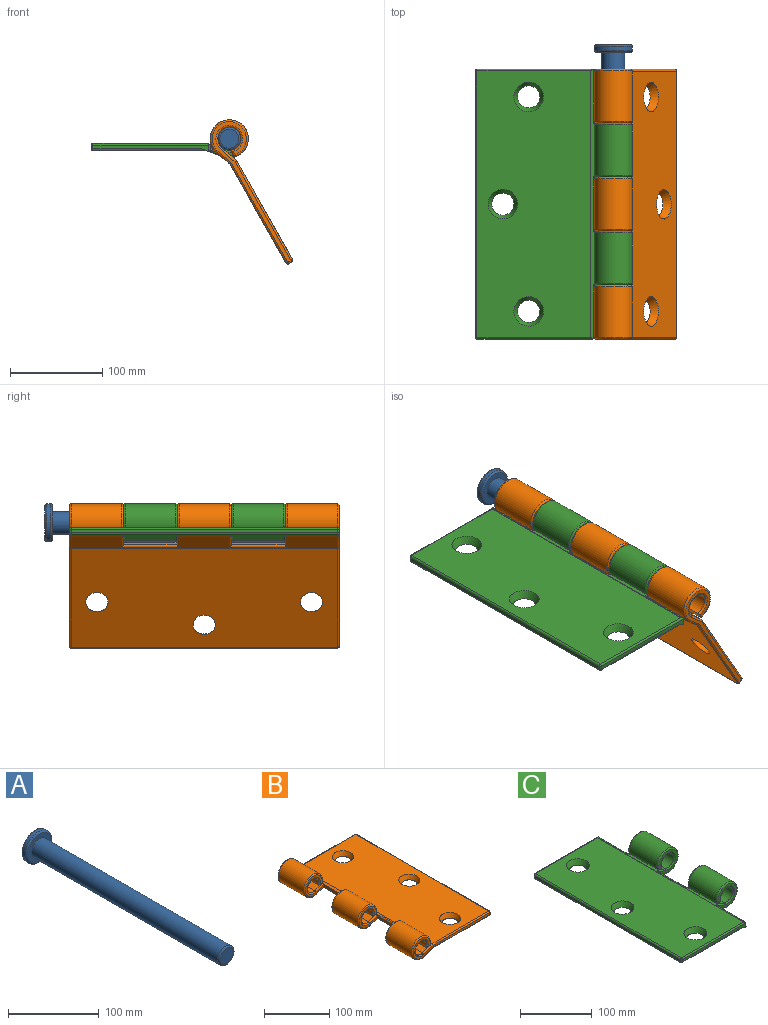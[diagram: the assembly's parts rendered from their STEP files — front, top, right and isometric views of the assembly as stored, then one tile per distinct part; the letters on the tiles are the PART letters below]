
ASSEMBLY  parts=3 mates=2
PART A: 8 faces, bbox 44.4x300x44.4 mm
  f0: cylinder r=12.25mm len=290mm, axis (0,1,0), area 22321mm2, adj f4,f7
  f1: plane 20.5x20.5mm, normal (0,-1,0), area 330.1mm2, adj f7
  f2: cylinder r=20.5mm len=41mm, axis (0,-1,0), area 515.2mm2, adj f5,f6
  f3: plane 37x37mm, normal (0,1,0), area 1075.2mm2, adj f6
  f4: plane 37x37mm, normal (0,-1,0), area 603.8mm2, adj f0,f5
  f5: torus R=18.5mm, axis (0,1,0), area 390.3mm2, adj f2,f4
  f6: torus R=18.5mm, axis (0,1,0), area 390.3mm2, adj f2,f3
  f7: torus R=10.25mm, axis (0,1,0), area 227.5mm2, adj f0,f1
PART B: 69 faces, bbox 171.7x292x44.4 mm
  f0: cylinder r=12.5mm len=54.4mm, axis (0,1,0), area 3703.3mm2, adj f4,f7,f27,f36
  f1: cylinder r=12.5mm len=54.4mm, axis (0,1,0), area 3703.3mm2, adj f5,f7,f35,f67
  f2: cylinder r=20.5mm len=54.4mm, axis (0,1,0), area 5913.6mm2, adj f4,f11,f25,f39
  f3: cylinder r=20.5mm len=54.4mm, axis (0,1,0), area 5913.6mm2, adj f5,f11,f32,f53
  f4: plane 56.4x8.42mm, normal (0,0,-1), area 473.3mm2, adj f0,f2,f24,f25,f27,f37
  f5: plane 56.4x8.42mm, normal (0,0,-1), area 473.3mm2, adj f1,f3,f21,f34,f53,f67
  f6: cylinder r=12.5mm len=54.4mm, axis (0,1,0), area 3703.3mm2, adj f7,f13,f41,f66
  f7: plane 288x20.54mm, normal (-0.32,0,0.95), area 3970.7mm2, adj f0,f1,f6,f8,f19,f29,f31,f33
  f8: plane 288x123mm, normal (0,0,1), area 33011.3mm2, adj f7,f16,f17,f18,f40,f47,f48
  f9: plane 288x4mm, normal (1,0,0), area 1152mm2, adj f46,f47,f51,f52
  f10: plane 288x123mm, normal (0,0,-1), area 34066.8mm2, adj f11,f16,f17,f18,f45,f51,f56
  f11: plane 288x17.59mm, normal (0.34,0,-0.94), area 3224.6mm2, adj f2,f3,f10,f12,f26,f28,f30,f42
  f12: cylinder r=20.5mm len=54.4mm, axis (0,1,0), area 5820.5mm2, adj f11,f60,f61,f62
  f13: plane 56.4x6.8mm, normal (0,0,-1), area 382.5mm2, adj f6,f15,f41,f60,f62,f65
  f14: plane 166x37mm, normal (0,-1,0), area 913.5mm2, adj f36,f37,f38,f39,f40,f42,f45,f46
  f15: plane 166x37mm, normal (0,1,0), area 921.7mm2, adj f13,f41,f44,f48,f52,f56,f58,f60
  f16: cone r=12mm half-angle=26.6deg, axis (0,0,1), area 786.8mm2, adj f8,f10
  f17: cone r=12mm half-angle=26.6deg, axis (0,0,1), area 786.8mm2, adj f8,f10
  f18: cone r=12mm half-angle=26.6deg, axis (0,0,1), area 786.8mm2, adj f8,f10
  f19: plane 62.4x5.26mm, normal (-1,0,0), area 308.8mm2, adj f7,f20,f21,f57,f64,f68
  f20: plane 39.12x37mm, normal (0,-1,0), area 406.2mm2, adj f19,f57,f59,f61,f64,f65,f66
  f21: plane 39.12x37mm, normal (0,1,0), area 414.5mm2, adj f5,f19,f53,f55,f57,f67,f68
  f22: plane 58.61x3.82mm, normal (-1,0,0), area 222.9mm2, adj f23,f24,f28,f29,f31,f33
  f23: plane 39.12x37mm, normal (0,-1,0), area 406.2mm2, adj f22,f28,f30,f32,f33,f34,f35
  f24: plane 39.12x37mm, normal (0,1,0), area 414.5mm2, adj f4,f22,f25,f26,f27,f28,f29
  f25: torus R=18.5mm, axis (0,1,0), area 330mm2, adj f2,f4,f24,f26
  f26: cylinder r=2mm len=16.94mm, axis (0.94,0,0.34), area 50.3mm2, adj f11,f24,f25,f28
  f27: torus R=14.5mm, axis (0,1,0), area 225.3mm2, adj f0,f4,f24,f29
  f28: cylinder r=2mm len=62.4mm, axis (0,1,0), area 228.2mm2, adj f11,f22,f23,f24,f26,f30
  f29: cylinder r=2mm len=18.54mm, axis (-0.95,0,-0.32), area 55.3mm2, adj f7,f22,f24,f27,f31
  f30: cylinder r=2mm len=16.94mm, axis (-0.94,0,-0.34), area 50.3mm2, adj f11,f23,f28,f32
  f31: cylinder r=2mm len=62.4mm, axis (0,-1,0), area 150.4mm2, adj f7,f22,f29,f33
  f32: torus R=18.5mm, axis (0,1,0), area 327.6mm2, adj f3,f23,f30,f34
  f33: cylinder r=2mm len=18.54mm, axis (0.95,0,0.32), area 55.3mm2, adj f7,f22,f23,f31,f35
  f34: cylinder r=2mm len=8.42mm, axis (-1,0,0), area 21.4mm2, adj f5,f23,f32,f35
  f35: torus R=14.5mm, axis (0,1,0), area 222.9mm2, adj f1,f23,f33,f34
  f36: torus R=14.5mm, axis (0,-1,0), area 222.9mm2, adj f0,f14,f37,f38
  f37: cylinder r=2mm len=8.42mm, axis (1,0,0), area 21.4mm2, adj f4,f14,f36,f39
  f38: cylinder r=2mm len=21.18mm, axis (-0.95,0,-0.32), area 67.7mm2, adj f7,f14,f36,f40
  f39: torus R=18.5mm, axis (0,-1,0), area 327.6mm2, adj f2,f14,f37,f42
  f40: cylinder r=2mm len=123mm, axis (-1,0,0), area 386mm2, adj f8,f14,f38,f43
  f41: torus R=14.5mm, axis (0,-1,0), area 225.3mm2, adj f6,f13,f15,f44
  f42: cylinder r=2mm len=18.59mm, axis (0.94,0,0.34), area 59.1mm2, adj f11,f14,f39,f45
  f43: sphere r=2mm, area 6.3mm2, adj f40,f46,f47
  f44: cylinder r=2mm len=21.18mm, axis (0.95,0,0.32), area 67.7mm2, adj f7,f15,f41,f48
  f45: cylinder r=2mm len=123.35mm, axis (1,0,0), area 386.8mm2, adj f10,f14,f42,f49
  f46: cylinder r=2mm len=4mm, axis (0,0,1), area 12.6mm2, adj f9,f14,f43,f49
  f47: cylinder r=2mm len=288mm, axis (0,1,0), area 904.8mm2, adj f8,f9,f43,f50
  f48: cylinder r=2mm len=123mm, axis (1,0,0), area 386mm2, adj f8,f15,f44,f50
  f49: sphere r=2mm, area 6.3mm2, adj f45,f46,f51
  f50: sphere r=2mm, area 6.3mm2, adj f47,f48,f52
  f51: cylinder r=2mm len=288mm, axis (0,1,0), area 904.8mm2, adj f9,f10,f49,f54
  f52: cylinder r=2mm len=4mm, axis (0,0,-1), area 12.6mm2, adj f9,f15,f50,f54
  f53: torus R=18.5mm, axis (0,1,0), area 330mm2, adj f3,f5,f21,f55
  f54: sphere r=2mm, area 6.3mm2, adj f51,f52,f56
  f55: cylinder r=2mm len=16.94mm, axis (0.94,0,0.34), area 50.3mm2, adj f11,f21,f53,f57
  f56: cylinder r=2mm len=123.35mm, axis (-1,0,0), area 386.8mm2, adj f10,f15,f54,f58
  f57: cylinder r=2mm len=62.4mm, axis (0,1,0), area 228.2mm2, adj f11,f19,f20,f21,f55,f59
  f58: cylinder r=2mm len=18.59mm, axis (-0.94,0,-0.34), area 59.1mm2, adj f11,f15,f56,f60
  f59: cylinder r=2mm len=16.94mm, axis (-0.94,0,-0.34), area 50.3mm2, adj f11,f20,f57,f61
  f60: torus R=18.5mm, axis (0,-1,0), area 328.3mm2, adj f12,f13,f15,f58,f62
  f61: torus R=18.5mm, axis (0,1,0), area 324.2mm2, adj f12,f20,f59,f63
  f62: cylinder r=2mm len=56.35mm, axis (0,1,0), area 156.4mm2, adj f12,f13,f60,f63
  f63: sphere r=2mm, area 5.6mm2, adj f61,f62,f65
  f64: cylinder r=2mm len=17.18mm, axis (0.95,0,0.32), area 54mm2, adj f7,f19,f20,f66
  f65: cylinder r=2mm len=6.8mm, axis (-1,0,0), area 18.1mm2, adj f13,f20,f63,f66
  f66: torus R=14.5mm, axis (0,1,0), area 222.9mm2, adj f6,f20,f64,f65
  f67: torus R=14.5mm, axis (0,1,0), area 225.3mm2, adj f1,f5,f21,f68
  f68: cylinder r=2mm len=17.18mm, axis (-0.95,0,-0.32), area 54mm2, adj f7,f19,f21,f67
PART C: 74 faces, bbox 171.7x292x44.4 mm
  f0: cylinder r=12.5mm len=54.4mm, axis (0,1,0), area 3703.3mm2, adj f2,f6,f27,f61
  f1: cylinder r=12.5mm len=54.4mm, axis (0,1,0), area 3703.3mm2, adj f2,f7,f33,f43
  f2: plane 291.31x20.23mm, normal (0.32,0,0.95), area 2780.8mm2, adj f0,f1,f28,f29,f30,f31,f32,f46
  f3: plane 292x23.17mm, normal (-0.34,0,-0.94), area 2310.2mm2, adj f4,f5,f8,f9,f12,f35,f36,f37
  f4: cylinder r=20.5mm len=54.4mm, axis (0,1,0), area 5913.6mm2, adj f3,f6,f34,f54
  f5: cylinder r=20.5mm len=54.4mm, axis (0,1,0), area 5913.6mm2, adj f3,f7,f40,f42
  f6: plane 56.4x8.42mm, normal (0,0,-1), area 473.3mm2, adj f0,f4,f19,f27,f34,f55
  f7: plane 56.4x8.42mm, normal (0,0,-1), area 473.3mm2, adj f1,f5,f20,f33,f40,f41
  f8: plane 125x6.59mm, normal (0,-1,0), area 510.3mm2, adj f3,f45,f50,f51,f57,f62
  f9: plane 125x6.59mm, normal (0,1,0), area 510.3mm2, adj f3,f53,f64,f69,f71,f72
  f10: plane 288x122.68mm, normal (0,0,1), area 32917.7mm2, adj f13,f14,f15,f62,f63,f67,f71
  f11: plane 288x4mm, normal (-1,0,0), area 1152mm2, adj f51,f52,f63,f64
  f12: plane 288x123mm, normal (0,0,-1), area 34066.8mm2, adj f3,f13,f14,f15,f45,f52,f53
  f13: cone r=12mm half-angle=26.6deg, axis (0,0,1), area 786.8mm2, adj f10,f12
  f14: cone r=12mm half-angle=26.6deg, axis (0,0,1), area 786.8mm2, adj f10,f12
  f15: cone r=12mm half-angle=26.6deg, axis (0,0,1), area 786.8mm2, adj f10,f12
  f16: plane 37x37mm, normal (0,-1,0), area 398.4mm2, adj f23,f41,f42,f43,f44,f46
  f17: plane 54.4x3.82mm, normal (1,0,0), area 207.6mm2, adj f23,f50,f56,f57
  f18: plane 54.4x3.82mm, normal (1,0,0), area 207.6mm2, adj f24,f25,f30,f37
  f19: plane 37x37mm, normal (0,-1,0), area 406.7mm2, adj f6,f24,f27,f28,f34,f35
  f20: plane 37x37mm, normal (0,1,0), area 406.7mm2, adj f7,f25,f32,f33,f39,f40
  f21: plane 37x37mm, normal (0,1,0), area 398.4mm2, adj f26,f54,f55,f60,f61,f66
  f22: plane 54.4x3.82mm, normal (1,0,0), area 207.6mm2, adj f26,f69,f72,f73
  f23: cylinder r=2mm len=5.25mm, axis (0,0,-1), area 12.1mm2, adj f16,f17,f47,f49
  f24: cylinder r=2mm len=5.25mm, axis (0,0,-1), area 12.1mm2, adj f18,f19,f29,f36
  f25: cylinder r=2mm len=5.25mm, axis (0,0,1), area 12.1mm2, adj f18,f20,f31,f38
  f26: cylinder r=2mm len=5.25mm, axis (0,0,1), area 12.1mm2, adj f21,f22,f65,f70
  f27: torus R=14.5mm, axis (0,-1,0), area 225.3mm2, adj f0,f6,f19,f28
  f28: cylinder r=2mm len=14.54mm, axis (0.95,0,-0.32), area 46.1mm2, adj f2,f19,f27,f29
  f29: bspline ~4.7x4.17mm, area 12.7mm2, adj f2,f24,f28,f30
  f30: cylinder r=2mm len=54.4mm, axis (0,1,0), area 135.9mm2, adj f2,f18,f29,f31
  f31: bspline ~4.7x4mm, area 12.7mm2, adj f2,f25,f30,f32
  f32: cylinder r=2mm len=14.54mm, axis (-0.95,0,0.32), area 46.1mm2, adj f2,f20,f31,f33
  f33: torus R=14.5mm, axis (0,-1,0), area 225.3mm2, adj f1,f7,f20,f32
  f34: torus R=18.5mm, axis (0,-1,0), area 330mm2, adj f4,f6,f19,f35
  f35: cylinder r=2mm len=12.94mm, axis (-0.94,0,0.34), area 40.9mm2, adj f3,f19,f34,f36
  f36: bspline ~5.02x4.17mm, area 15.5mm2, adj f3,f24,f35,f37
  f37: cylinder r=2mm len=54.4mm, axis (0,-1,0), area 208.3mm2, adj f3,f18,f36,f38
  f38: bspline ~5.02x4mm, area 15.5mm2, adj f3,f25,f37,f39
  f39: cylinder r=2mm len=12.94mm, axis (0.94,0,-0.34), area 40.9mm2, adj f3,f20,f38,f40
  f40: torus R=18.5mm, axis (0,-1,0), area 330mm2, adj f5,f7,f20,f39
  f41: cylinder r=2mm len=8.42mm, axis (-1,0,0), area 21.4mm2, adj f7,f16,f42,f43
  f42: torus R=18.5mm, axis (0,-1,0), area 327.6mm2, adj f5,f16,f41,f44
  f43: torus R=14.5mm, axis (0,-1,0), area 222.9mm2, adj f1,f16,f41,f46
  f44: cylinder r=2mm len=12.94mm, axis (-0.94,0,0.34), area 40.9mm2, adj f3,f16,f42,f47
  f45: cylinder r=2mm len=123mm, axis (-1,0,0), area 380mm2, adj f3,f8,f12,f48
  f46: cylinder r=2mm len=14.54mm, axis (0.95,0,-0.32), area 46.1mm2, adj f2,f16,f43,f49
  f47: bspline ~5.02x4.17mm, area 15.5mm2, adj f3,f23,f44,f50
  f48: sphere r=2mm, area 6.3mm2, adj f45,f51,f52
  f49: bspline ~4.7x4.17mm, area 12.7mm2, adj f2,f23,f46,f56
  f50: cylinder r=2mm len=56.4mm, axis (0,-1,0), area 213.7mm2, adj f3,f8,f17,f47,f57
  f51: cylinder r=2mm len=4mm, axis (0,0,1), area 12.6mm2, adj f8,f11,f48,f58
  f52: cylinder r=2mm len=288mm, axis (0,1,0), area 904.8mm2, adj f11,f12,f48,f59
  f53: cylinder r=2mm len=123mm, axis (1,0,0), area 380mm2, adj f3,f9,f12,f59
  f54: torus R=18.5mm, axis (0,-1,0), area 327.6mm2, adj f4,f21,f55,f60
  f55: cylinder r=2mm len=8.42mm, axis (1,0,0), area 21.4mm2, adj f6,f21,f54,f61
  f56: cylinder r=2mm len=56.15mm, axis (0,1,0), area 138.5mm2, adj f2,f17,f49,f57,f62
  f57: cylinder r=2mm len=7.56mm, axis (0,0,1), area 19.3mm2, adj f8,f17,f50,f56,f62
  f58: sphere r=2mm, area 6.3mm2, adj f51,f62,f63
  f59: sphere r=2mm, area 6.3mm2, adj f52,f53,f64
  f60: cylinder r=2mm len=12.94mm, axis (0.94,0,-0.34), area 40.9mm2, adj f3,f21,f54,f65
  f61: torus R=14.5mm, axis (0,-1,0), area 222.9mm2, adj f0,f21,f55,f66
  f62: cylinder r=2mm len=125.97mm, axis (1,0,0), area 391.1mm2, adj f2,f8,f10,f56,f57,f58,f67
  f63: cylinder r=2mm len=288mm, axis (0,1,0), area 904.8mm2, adj f10,f11,f58,f68
  f64: cylinder r=2mm len=4mm, axis (0,0,-1), area 12.6mm2, adj f9,f11,f59,f68
  f65: bspline ~5.02x4mm, area 15.5mm2, adj f3,f26,f60,f69
  f66: cylinder r=2mm len=14.54mm, axis (-0.95,0,0.32), area 46.1mm2, adj f2,f21,f61,f70
  f67: cylinder r=2mm len=289.27mm, axis (0,-1,0), area 186mm2, adj f2,f10,f62,f71
  f68: sphere r=2mm, area 6.3mm2, adj f63,f64,f71
  f69: cylinder r=2mm len=56.4mm, axis (0,-1,0), area 213.7mm2, adj f3,f9,f22,f65,f72
  f70: bspline ~4.7x4mm, area 12.7mm2, adj f2,f26,f66,f73
  f71: cylinder r=2mm len=125.97mm, axis (-1,0,0), area 391.1mm2, adj f2,f9,f10,f67,f68,f72,f73
  f72: cylinder r=2mm len=7.56mm, axis (0,0,-1), area 19.3mm2, adj f9,f22,f69,f71,f73
  f73: cylinder r=2mm len=56.15mm, axis (0,1,0), area 138.5mm2, adj f2,f22,f70,f71,f72
PLACE A rot(axis=(0,1,0),60.4deg) t=(-21.95,124.62,19.85)mm
PLACE B rot(axis=(0,1,0),60.4deg) t=(-21.95,106.26,19.85)mm
PLACE C t=(-30,106.26,-3.99)mm fixed
MATE revolute C.f0 <-> B.f53  axis (0,-1,0) through (-5.5,-10.54,1.01)mm
MATE slider A.f0 <-> B.f0  axis (0,-1,0) through (-5.5,-167.38,1.01)mm
